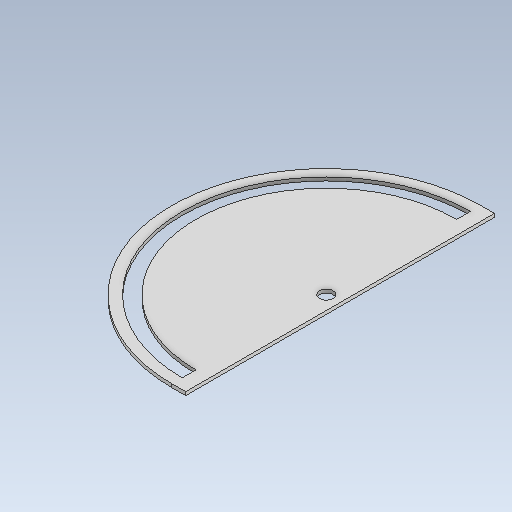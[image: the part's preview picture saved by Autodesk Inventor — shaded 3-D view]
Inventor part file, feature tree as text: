
AUTODESK INVENTOR PART (.ipt)
format: ipt  version: 2020.2 (Build 242310000, 310)  size: 121,856 bytes
history: native  units: in
note: dims shown in document units (in); Inventor stores cm internally (conversion verified against a paired STEP export)
features: extrude x1, sketch x1
ambient origin geometry x8: Origin, YZ Plane, XZ Plane, XY Plane, X Axis, Y Axis, Z Axis, Center Point
bodies: Solid1 (feature_tree)
feature tree (2):
  extrude  "Extrusion1"  Depth=0.0394in
  sketch  "Sketch1"  dims[d0=0.1575in d1=2.9921in d2=1.4961in d3=3.3071in d4=0.1575in d5=180.0deg d6=3.3071in d7=3.5433in d8=1.7717in d9=0.1575in d10=180.0deg d11=0.1181in d12=90.0deg d13=0.0394in d14=0.0in]
